# Revit family: Credenza-Freestanding-Teknion-JNFC_Mobile_Credenza-R2018
name_source: partatom
category: Furniture
revit_build: Autodesk Revit 2018 (Build: 20190510_1515(x64)
units: mm (PartAtom-declared; Revit-internal decimal feet)

## family parameters
Always vertical = Yes
Cut with Voids When Loaded = No
OmniClass Number = 23.40.20.00
OmniClass Title = General Furniture and Specialties
Room Calculation Point = No
Shared = Yes
Work Plane-Based = No

## types (6) — shared parameters
Assembly Code = E2020200
Manufacturer = Teknion
Manufacturer Fax = 416.661.4586
Part Number = JNFC
Product Documentation Link = https://www.teknion.com
Product Line = Expansion Cityline
Product Page URL = https://www.teknion.com
Series = Expansion Cityline
Sustainability Data = https://www.teknion.com
URL = www.teknion.com
Unit Weight URL = http://www.teknion.com
Warranty = http://www.teknion.com

## per-type parameters (varying)
| type | Center Divide | Description | Handle offset Solid | Handle offset metal | Left Drawer | Model | Right Drawer | Width |
| 36" Widith, Dawers on Left | 18.614 " | Mobile Credenza, Small Box, File & Open Section Configuration, 23" Height, 18" Depth, 36" Width, Drawers on the Left | 7.022 " | 7.03 " | Yes | JNFC_DO231836L | No | 36 " |
| 36" Width, Drawers on Right | 16.685 " | Mobile Credenza, Small Box, File & Open Section Configuration, 23" Height, 18" Depth, 36" Width, Drawers on the Right | 7.022 " | 7.03 " | No | JNFC_DO231836R | Yes | 36 " |
| 42" Width, Drawers on Right | 18 " | Mobile Credenza, Small Box, File & Open Section Configuration, 23" Height, 18" Depth, 42" Width, Drawers on the Right | 9.364 " | 9.372 " | No | JNFC_DO231842R | Yes | 42 " |
| 42" Width, Drawers on Left | 23.299 " | Mobile Credenza, Small Box, File & Open Section Configuration, 23" Height, 18" Depth, 42" Width, Drawers on the Left | 9.364 " | 9.372 " | Yes | JNFC_DO231842L | No | 42 " |
| 48" Width, Drawers on Right | 18 " | Mobile Credenza, Small Box, File & Open Section Configuration, 23" Height, 18" Depth, 48" Width, Drawers on the Right | 12.364 " | 12.372 " | No | JNFC_DO231848R | Yes | 48 " |
| 48" Width, Drawers on Left | 29.299 " | Mobile Credenza, Small Box, File & Open Section Configuration, 23" Height, 18" Depth, 48" Width, Drawers on the Left | 12.364 " | 12.372 " | Yes | JNFC_DO231848L | No | 48 " |

## geometry (parser evidence)
native form markers: Sweep x2
no freeform markers — native parametric forms only
